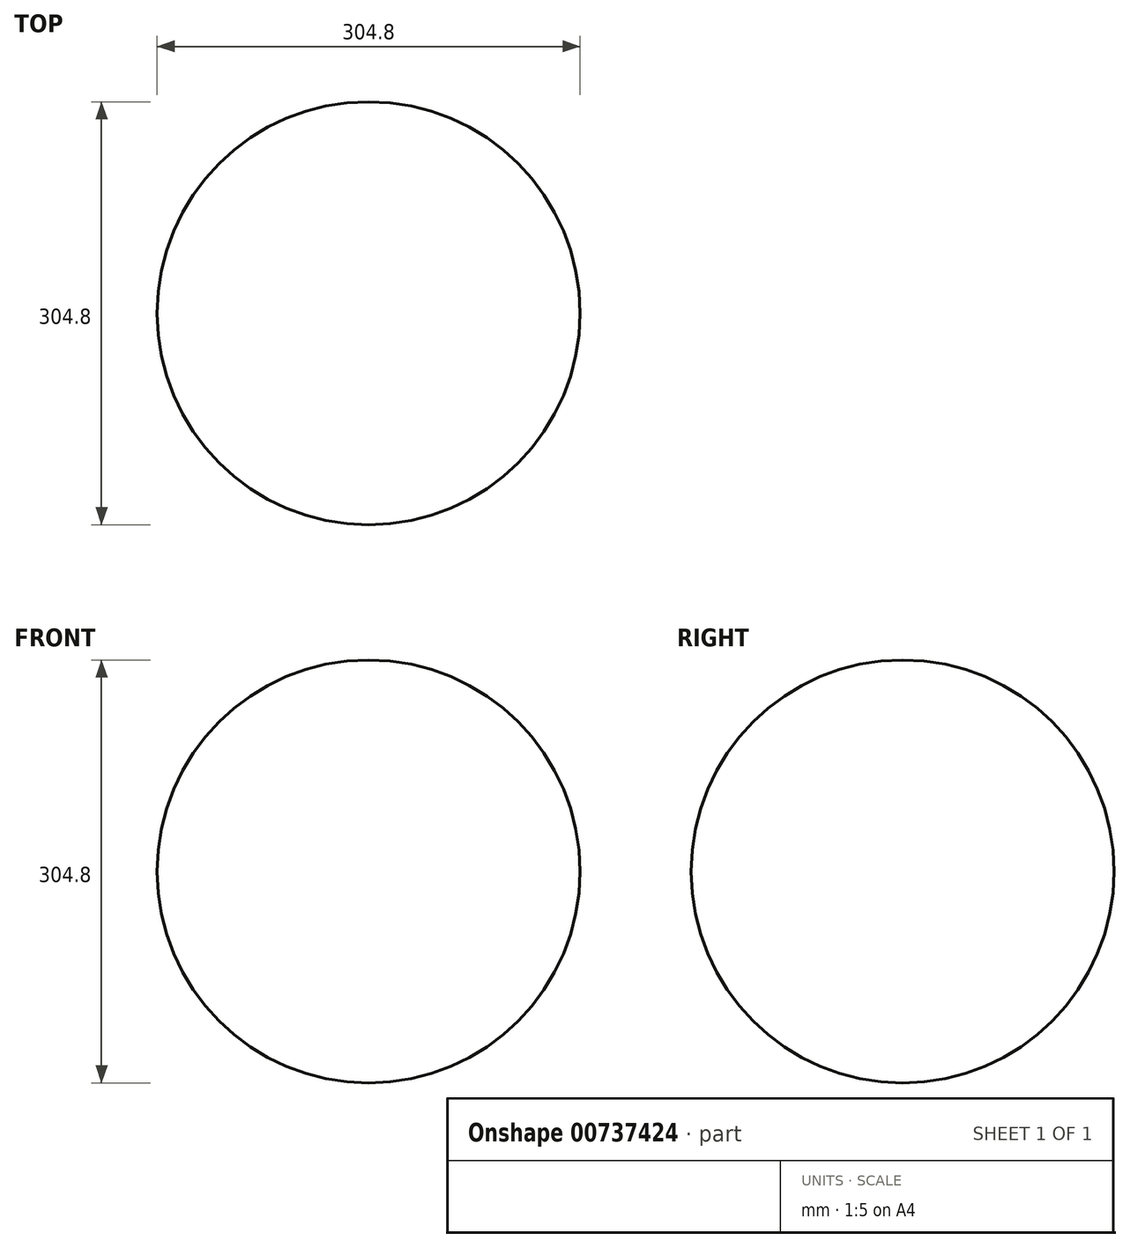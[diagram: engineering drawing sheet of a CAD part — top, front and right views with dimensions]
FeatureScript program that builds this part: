
annotation { "Feature Type Name" : "Feature", "Feature Type Description" : "" }
export const myFeature = defineFeature(function(context is Context, id is Id, definition is map)
    precondition{}
    {
        {
            var Q0;
            Q0=qCreatedBy(makeId("Front.planeOp"),FACE);
            var sketch = newSketch(context, id + "F0", { "sketchPlane" : qUnion([Q0])});
            skLineSegment(sketch, "E0", {"start": v(0, 0) * mm, "end": v(0, 177.8) * mm, "construction": true});
            skArc(sketch, "E1", {"start": v(152.4, 177.8) * mm, "mid": v(0, 330.2) * mm, "end": v(-152.4, 177.8) * mm});
            skLineSegment(sketch, "E2", {"start": v(0, 177.8) * mm, "end": v(152.4, 177.8) * mm});
            skLineSegment(sketch, "E3", {"start": v(152.4, 177.8) * mm, "end": v(-152.4, 177.8) * mm});
            skSolve(sketch);
        }
        {
            var Q0;
            {var subQ0=sQuery(id+"F0.wireOp",EDGE,"E1");Q0=makeQuery(id+"F0.imprint","IMPRINT",FACE,{"disambiguationData":[TD([[makeQuery(id+"F0.imprint","IMPRINT",EDGE,{"derivedFrom":subQ0}),1.0]])]});}
            var Q1;
            Q1=sQuery(id+"F0.wireOp",EDGE,"E3");
            revolve(context, id + "F1", {"surfaceOperationType" : NewSurfaceOperationType.NEW, "entities" : qUnion([Q0]), "axis" : qUnion([Q1]), "revolveType" : RevolveType.FULL});
        }
    });
